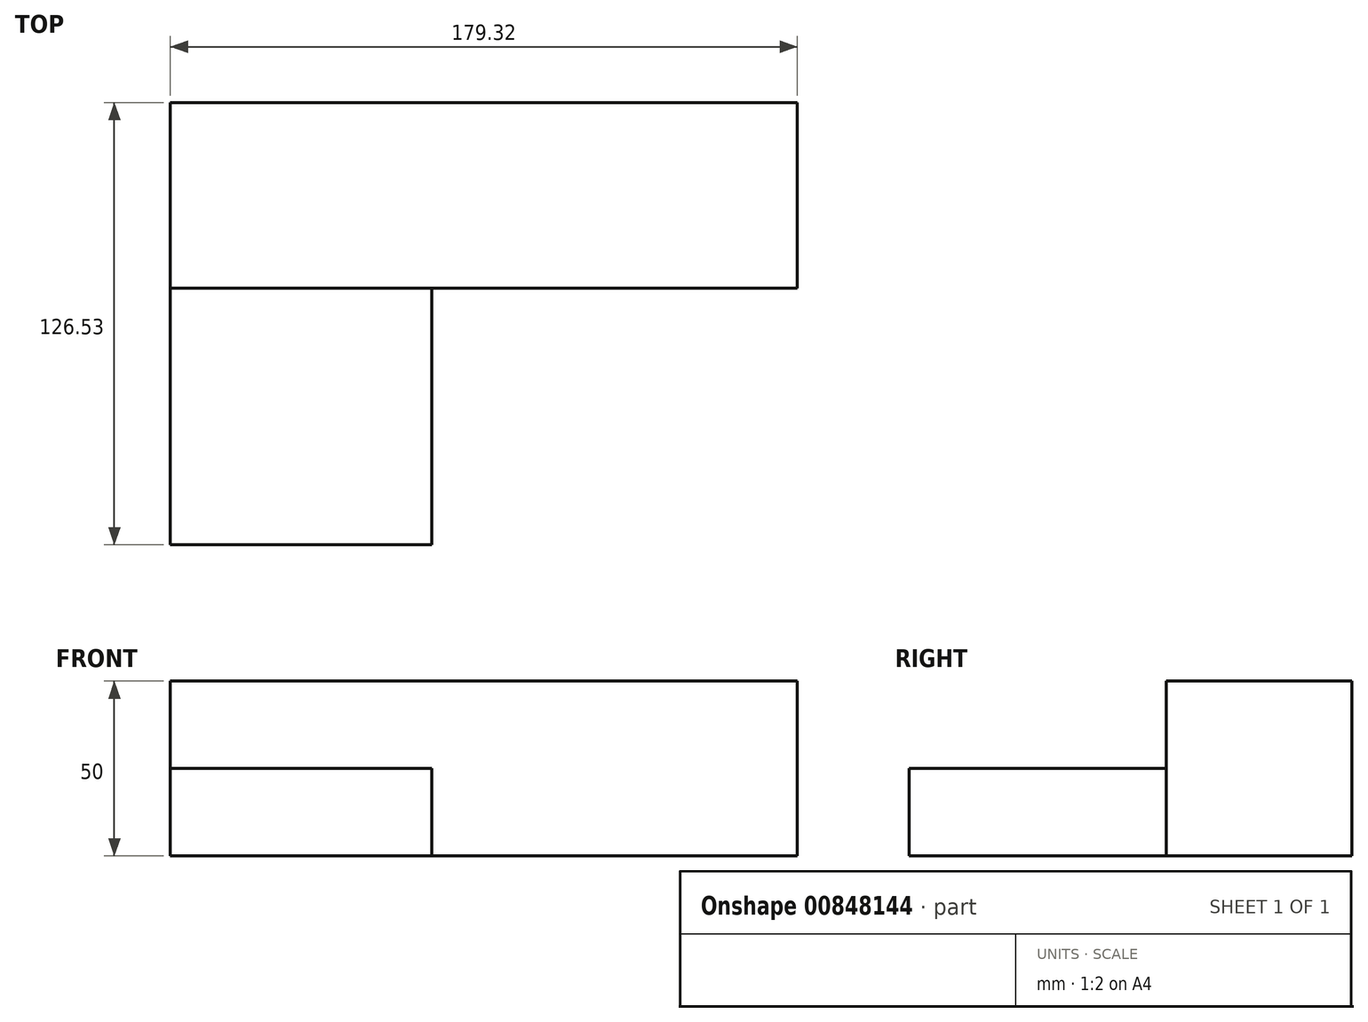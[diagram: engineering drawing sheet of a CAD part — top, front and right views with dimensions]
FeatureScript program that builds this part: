
annotation { "Feature Type Name" : "Feature", "Feature Type Description" : "" }
export const myFeature = defineFeature(function(context is Context, id is Id, definition is map)
    precondition{}
    {
        {
            var Q0;
            Q0=qCreatedBy(makeId("Top.planeOp"),FACE);
            var sketch = newSketch(context, id + "F0", { "sketchPlane" : qUnion([Q0])});
            skLineSegment(sketch, "E0.bottom", {"start": v(89.66, 26.52) * mm, "end": v(-89.66, 26.52) * mm});
            skLineSegment(sketch, "E0.top", {"start": v(89.66, -26.52) * mm, "end": v(-89.66, -26.52) * mm});
            skLineSegment(sketch, "E0.left", {"start": v(89.66, 26.52) * mm, "end": v(89.66, -26.52) * mm});
            skLineSegment(sketch, "E0.right", {"start": v(-89.66, 26.52) * mm, "end": v(-89.66, -26.52) * mm});
            skPoint(sketch, "E0.middle", {"position": v(0, 0) * mm});
            skLineSegment(sketch, "E1.bottom", {"start": v(-89.66, 26.52) * mm, "end": v(-14.89, 26.52) * mm});
            skLineSegment(sketch, "E1.top", {"start": v(-89.66, -100.01) * mm, "end": v(-14.89, -100.01) * mm});
            skLineSegment(sketch, "E1.left", {"start": v(-89.66, 26.52) * mm, "end": v(-89.66, -100.01) * mm});
            skLineSegment(sketch, "E1.right", {"start": v(-14.89, 26.52) * mm, "end": v(-14.89, -100.01) * mm});
            skSolve(sketch);
        }
        {
            var Q0;
            {var subQ0=sQuery(id+"F0.wireOp",EDGE,"E0.bottom");Q0=makeQuery(id+"F0.imprint","IMPRINT",FACE,{"disambiguationData":[TD([[makeQuery(id+"F0.imprint","IMPRINT",EDGE,{"derivedFrom":subQ0}),1.0]])]});}
            var Q1;
            {var subQ5=sQuery(id+"F0.wireOp",EDGE,"E1.bottom");Q1=makeQuery(id+"F0.imprint","IMPRINT",FACE,{"disambiguationData":[TD([[makeQuery(id+"F0.imprint","IMPRINT",EDGE,{"derivedFrom":subQ5}),-1.0]])]});}
            extrude(context, id + "F1", {"entities" : qUnion([Q0, Q1]), "depth" : 50 * mm, "offsetDistance" : 25 * mm});
        }
        {
            var Q0;
            {var subQ5=sQuery(id+"F0.wireOp",EDGE,"E1.top");Q0=makeQuery(id+"F0.imprint","IMPRINT",FACE,{"disambiguationData":[TD([[makeQuery(id+"F0.imprint","IMPRINT",EDGE,{"derivedFrom":subQ5}),1.0]])]});}
            extrude(context, id + "F2", {"entities" : qUnion([Q0]), "operationType" : NewBodyOperationType.ADD, "depth" : 25 * mm, "offsetDistance" : 25 * mm});
        }
    });
